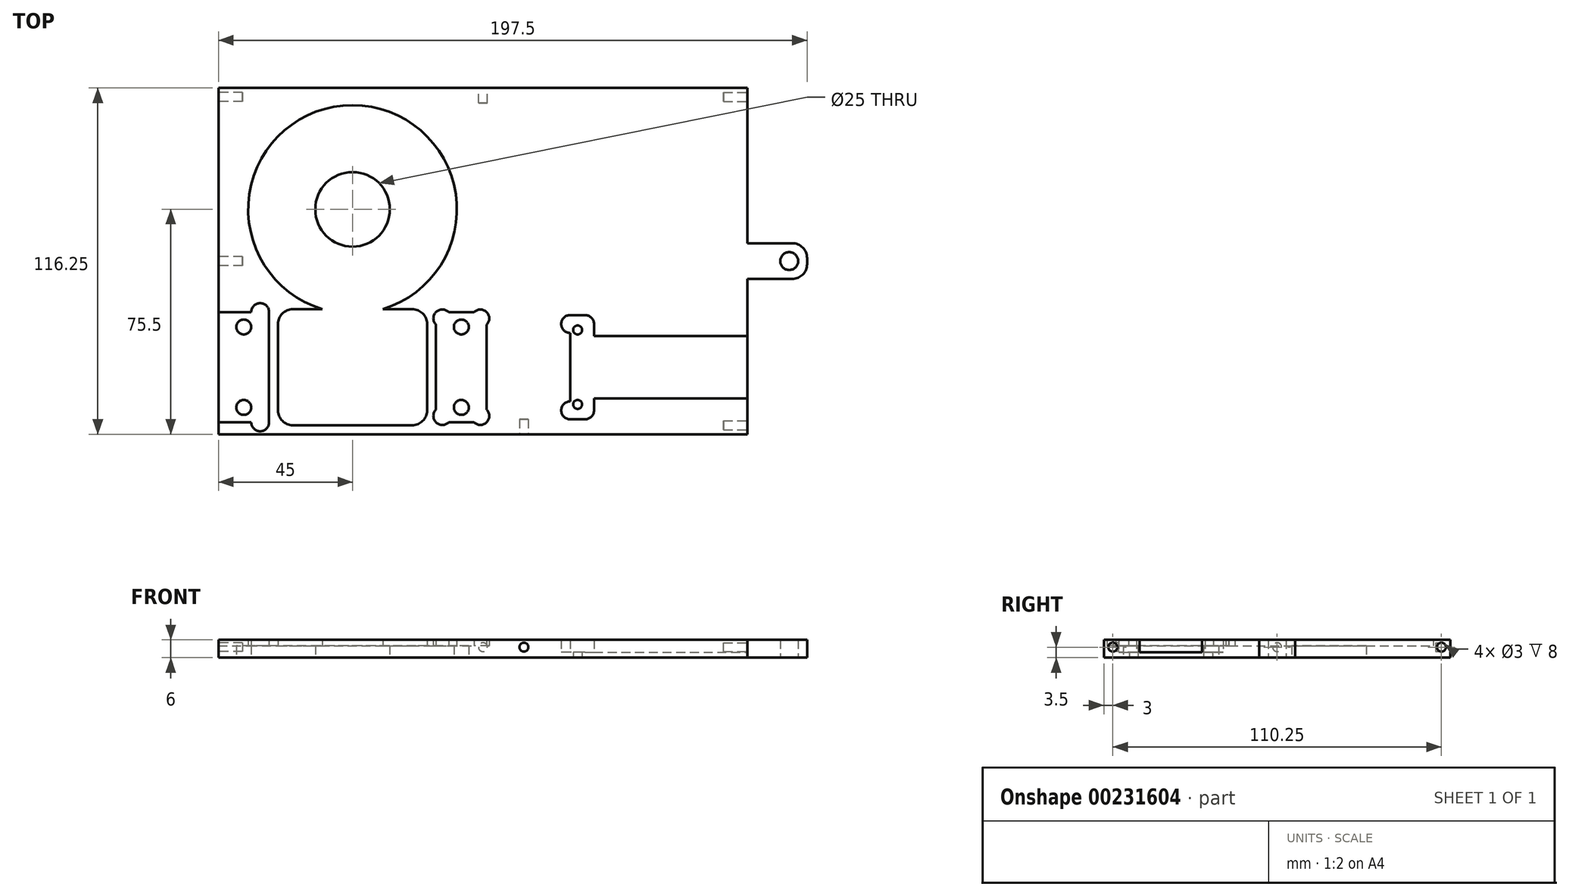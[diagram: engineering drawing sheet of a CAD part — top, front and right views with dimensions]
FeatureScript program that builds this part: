
annotation { "Feature Type Name" : "Feature", "Feature Type Description" : "" }
export const myFeature = defineFeature(function(context is Context, id is Id, definition is map)
    precondition{}
    {
        {
            var Q0;
            Q0=qCreatedBy(makeId("Top.planeOp"),FACE);
            var sketch = newSketch(context, id + "F0", { "sketchPlane" : qUnion([Q0])});
            skLineSegment(sketch, "E0.bottom", {"start": v(0, 0) * mm, "end": v(177.5, 0) * mm});
            skLineSegment(sketch, "E0.top", {"start": v(0, 116.25) * mm, "end": v(177.5, 116.25) * mm});
            skLineSegment(sketch, "E0.left", {"start": v(0, 0) * mm, "end": v(0, 116.25) * mm});
            skLineSegment(sketch, "E0.right", {"start": v(177.5, 0) * mm, "end": v(177.5, 116.25) * mm});
            skCircle(sketch, "E1", {"center": v(45, 75.5) * mm, "radius": 35 * mm});
            skLineSegment(sketch, "E2.right", {"start": v(177.5, 40) * mm, "end": v(177.5, 5) * mm});
            skCircle(sketch, "E3", {"center": v(191.5, 58.12) * mm, "radius": 3 * mm});
            skPoint(sketch, "E3.centerSnap1", {"position": v(191.5, -16.13) * mm});
            skPoint(sketch, "E4", {"position": v(177.5, 22.5) * mm});
            skLineSegment(sketch, "E5.bottom", {"start": v(25, 42) * mm, "end": v(65, 42) * mm});
            skLineSegment(sketch, "E5.top", {"start": v(25, 3) * mm, "end": v(65, 3) * mm});
            skLineSegment(sketch, "E5.left", {"start": v(20, 37) * mm, "end": v(20, 8) * mm});
            skLineSegment(sketch, "E5.right", {"start": v(70, 37) * mm, "end": v(70, 8) * mm});
            skLineSegment(sketch, "E6", {"start": v(70, 22.5) * mm, "end": v(20, 22.5) * mm, "construction": true});
            skLineSegment(sketch, "E7", {"start": v(45, 3) * mm, "end": v(45, 42) * mm, "construction": true});
            skCircle(sketch, "E8", {"center": v(45, 75.5) * mm, "radius": 12.5 * mm});
            skLineSegment(sketch, "E9.bottom", {"start": v(0, 4) * mm, "end": v(11, 4) * mm});
            skLineSegment(sketch, "E9.top", {"start": v(0, 41) * mm, "end": v(11, 41) * mm});
            skLineSegment(sketch, "E9.left", {"start": v(0, 4) * mm, "end": v(0, 41) * mm});
            skLineSegment(sketch, "E9.right", {"start": v(17, 4) * mm, "end": v(17, 41) * mm});
            skPoint(sketch, "E10", {"position": v(17, 22.5) * mm});
            skLineSegment(sketch, "E11.bottom", {"start": v(72.07, 41) * mm, "end": v(73, 41) * mm});
            skLineSegment(sketch, "E11.top", {"start": v(72.07, 4) * mm, "end": v(73, 4) * mm});
            skLineSegment(sketch, "E11.left", {"start": v(73, 36.76) * mm, "end": v(73, 8.24) * mm});
            skLineSegment(sketch, "E11.right", {"start": v(90, 36.76) * mm, "end": v(90, 8.24) * mm});
            skPoint(sketch, "E12", {"position": v(90, 22.5) * mm});
            skLineSegment(sketch, "E13", {"start": v(73, 4) * mm, "end": v(72.07, 4) * mm, "construction": true});
            skLineSegment(sketch, "E14", {"start": v(70, 4) * mm, "end": v(70, 41) * mm, "construction": true});
            skLineSegment(sketch, "E15", {"start": v(70, 41) * mm, "end": v(73, 41) * mm, "construction": true});
            skLineSegment(sketch, "E16", {"start": v(90, 41) * mm, "end": v(93, 41) * mm, "construction": true});
            skLineSegment(sketch, "E17", {"start": v(93, 41) * mm, "end": v(93, 4) * mm, "construction": true});
            skLineSegment(sketch, "E18", {"start": v(93, 4) * mm, "end": v(90, 4) * mm, "construction": true});
            skLineSegment(sketch, "E19.bottom", {"start": v(90, 13.5) * mm, "end": v(115, 13.5) * mm, "construction": true});
            skLineSegment(sketch, "E19.top", {"start": v(90, 31.5) * mm, "end": v(115, 31.5) * mm, "construction": true});
            skLineSegment(sketch, "E19.left", {"start": v(90, 13.5) * mm, "end": v(90, 31.5) * mm, "construction": true});
            skLineSegment(sketch, "E19.right", {"start": v(115, 13.5) * mm, "end": v(115, 31.5) * mm, "construction": true});
            skPoint(sketch, "E20", {"position": v(115, 22.5) * mm});
            skPoint(sketch, "E21", {"position": v(117.97, 22.5) * mm});
            skPoint(sketch, "E22", {"position": v(177.5, 58.12) * mm});
            skLineSegment(sketch, "E23.bottom", {"start": v(177.5, 64.12) * mm, "end": v(197.5, 64.12) * mm});
            skLineSegment(sketch, "E23.top", {"start": v(177.5, 52.12) * mm, "end": v(197.5, 52.12) * mm});
            skLineSegment(sketch, "E23.left", {"start": v(177.5, 64.12) * mm, "end": v(177.5, 52.13) * mm});
            skLineSegment(sketch, "E23.right", {"start": v(197.5, 64.12) * mm, "end": v(197.5, 52.12) * mm});
            skCircle(sketch, "E24", {"center": v(120.5, 10) * mm, "radius": 1.5 * mm});
            skCircle(sketch, "E25", {"center": v(120.5, 35) * mm, "radius": 1.5 * mm});
            skLineSegment(sketch, "E26", {"start": v(81.5, 41) * mm, "end": v(81.5, 4) * mm, "construction": true});
            skLineSegment(sketch, "E27", {"start": v(8.5, 41) * mm, "end": v(8.5, 4) * mm, "construction": true});
            skCircle(sketch, "E28", {"center": v(8.5, 36) * mm, "radius": 2.5 * mm});
            skCircle(sketch, "E29", {"center": v(8.5, 9) * mm, "radius": 2.5 * mm});
            skCircle(sketch, "E30", {"center": v(81.5, 36) * mm, "radius": 2.5 * mm});
            skCircle(sketch, "E31", {"center": v(81.5, 9) * mm, "radius": 2.5 * mm});
            skLineSegment(sketch, "E32", {"start": v(76.54, 37.46) * mm, "end": v(73, 41) * mm, "construction": true});
            skLineSegment(sketch, "E33", {"start": v(90, 22.5) * mm, "end": v(81.5, 22.5) * mm, "construction": true});
            skLineSegment(sketch, "E34", {"start": v(17, 41) * mm, "end": v(9.3, 33.3) * mm, "construction": true});
            skPoint(sketch, "E35.orphan", {"position": v(17, 4) * mm});
            skPoint(sketch, "E36.visualSharp", {"position": v(20, 42) * mm});
            skArc(sketch, "E36.filletArc", {"start": v(25, 42) * mm, "mid": v(21.46, 40.54) * mm, "end": v(20, 37) * mm});
            skPoint(sketch, "E37.visualSharp", {"position": v(70, 42) * mm});
            skArc(sketch, "E37.filletArc", {"start": v(70, 37) * mm, "mid": v(68.54, 40.54) * mm, "end": v(65, 42) * mm});
            skPoint(sketch, "E38.visualSharp", {"position": v(70, 3) * mm});
            skArc(sketch, "E38.filletArc", {"start": v(65, 3) * mm, "mid": v(68.54, 4.46) * mm, "end": v(70, 8) * mm});
            skPoint(sketch, "E39.visualSharp", {"position": v(20, 3) * mm});
            skArc(sketch, "E39.filletArc", {"start": v(20, 8) * mm, "mid": v(21.46, 4.46) * mm, "end": v(25, 3) * mm});
            skCircle(sketch, "E40", {"center": v(45, 75.5) * mm, "radius": 38.75 * mm, "construction": true});
            skPoint(sketch, "E41", {"position": v(45, 114.25) * mm});
            skPoint(sketch, "E42", {"position": v(6.25, 75.5) * mm});
            skPoint(sketch, "E43.orphan", {"position": v(17, 33.43) * mm});
            skPoint(sketch, "E44.orphan", {"position": v(17, 11.57) * mm});
            skArc(sketch, "E45.trimOffspring", {"start": v(17, 41) * mm, "mid": v(14, 44) * mm, "end": v(11, 41) * mm});
            skArc(sketch, "E46.trimOffspring", {"start": v(11, 4) * mm, "mid": v(14, 1) * mm, "end": v(17, 4) * mm});
            skArc(sketch, "E47", {"start": v(77.24, 41) * mm, "mid": v(73, 41) * mm, "end": v(73, 36.76) * mm});
            skPoint(sketch, "E48.orphan", {"position": v(73, 34.71) * mm});
            skLineSegment(sketch, "E49.trimOffspring", {"start": v(77.24, 41) * mm, "end": v(85.76, 41) * mm});
            skPoint(sketch, "E50.orphan", {"position": v(73, 22.5) * mm});
            skArc(sketch, "E51.MirrorCS", {"start": v(77.24, 4) * mm, "mid": v(73, 4) * mm, "end": v(73, 8.24) * mm});
            skArc(sketch, "E52.MirrorCS", {"start": v(85.76, 41) * mm, "mid": v(90, 41) * mm, "end": v(90, 36.76) * mm});
            skArc(sketch, "E53.MirrorCS", {"start": v(85.76, 4) * mm, "mid": v(90, 4) * mm, "end": v(90, 8.24) * mm});
            skPoint(sketch, "E54.orphan", {"position": v(73, 10.29) * mm});
            skPoint(sketch, "E55.orphan", {"position": v(90, 10.29) * mm});
            skPoint(sketch, "E56.orphan", {"position": v(90, 34.71) * mm});
            skLineSegment(sketch, "E57.trimOffspring", {"start": v(90, 41) * mm, "end": v(90.93, 41) * mm});
            skLineSegment(sketch, "E58.trimOffspring", {"start": v(90, 4) * mm, "end": v(90.93, 4) * mm});
            skLineSegment(sketch, "E59.trimOffspring", {"start": v(77.24, 4) * mm, "end": v(85.76, 4) * mm});
            skLineSegment(sketch, "E60", {"start": v(123, 40) * mm, "end": v(123, 11) * mm, "construction": true});
            skLineSegment(sketch, "E61", {"start": v(123, 40) * mm, "end": v(118, 40) * mm});
            skLineSegment(sketch, "E62", {"start": v(123, 5) * mm, "end": v(118, 5) * mm});
            skLineSegment(sketch, "E63", {"start": v(120.5, 5) * mm, "end": v(120.5, 40) * mm, "construction": true});
            skArc(sketch, "E64", {"start": v(118, 11) * mm, "mid": v(115, 8) * mm, "end": v(118, 5) * mm});
            skLineSegment(sketch, "E65.trimOffspring", {"start": v(118, 34) * mm, "end": v(118, 11) * mm});
            skArc(sketch, "E66.trimOffspring", {"start": v(118, 40) * mm, "mid": v(115, 37) * mm, "end": v(118, 34) * mm});
            skArc(sketch, "E67", {"start": v(126, 37) * mm, "mid": v(125.12, 39.12) * mm, "end": v(123, 40) * mm});
            skArc(sketch, "E68", {"start": v(123, 5) * mm, "mid": v(125.12, 5.88) * mm, "end": v(126, 8) * mm});
            skLineSegment(sketch, "E69", {"start": v(126, 12) * mm, "end": v(177.5, 12) * mm});
            skLineSegment(sketch, "E70", {"start": v(126, 33) * mm, "end": v(177.5, 33) * mm});
            skLineSegment(sketch, "E71", {"start": v(123, 34) * mm, "end": v(123, 33) * mm});
            skLineSegment(sketch, "E72", {"start": v(123, 12) * mm, "end": v(123, 11) * mm});
            skLineSegment(sketch, "E73.trimOffspring", {"start": v(123, 8) * mm, "end": v(123, 5) * mm, "construction": true});
            skLineSegment(sketch, "E74", {"start": v(126, 37) * mm, "end": v(126, 33) * mm});
            skLineSegment(sketch, "E75", {"start": v(126, 8) * mm, "end": v(126, 12) * mm});
            skSolve(sketch);
        }
        {
            var Q0;
            Q0=makeQuery(id+"F0.imprint","IMPRINT",FACE,{"disambiguationData":[TD([[makeQuery(id+"F0.imprint","IMPRINT",EDGE,{"derivedFrom":sQuery(id+"F0.wireOp",EDGE,"E0.bottom")}),1.0]])]});
            var Q1;
            Q1=makeQuery(id+"F0.imprint","IMPRINT",FACE,{"disambiguationData":[TD([[makeQuery(id+"F0.imprint","IMPRINT",EDGE,{"derivedFrom":sQuery(id+"F0.wireOp",EDGE,"E3")}),-1.0]])]});
            var Q2;
            {var subQ13=sQuery(id+"F0.wireOp",EDGE,"E0.top");Q2=makeQuery(id+"F0.imprint","IMPRINT",FACE,{"disambiguationData":[TD([[makeQuery(id+"F0.imprint","IMPRINT",EDGE,{"derivedFrom":subQ13}),-1.0]])]});}
            extrude(context, id + "F1", {"entities" : qUnion([Q0, Q1, Q2]), "depth" : 6 * mm});
        }
        {
            var Q0;
            Q0=makeQuery(id+"F0.imprint","IMPRINT",FACE,{"disambiguationData":[TD([[makeQuery(id+"F0.imprint","IMPRINT",EDGE,{"derivedFrom":sQuery(id+"F0.wireOp",EDGE,"E1")}),1.0]])]});
            var Q1;
            Q1=makeQuery(id+"F0.imprint","IMPRINT",FACE,{"disambiguationData":[TD([[makeQuery(id+"F0.imprint","IMPRINT",EDGE,{"derivedFrom":sQuery(id+"F0.wireOp",EDGE,"E8")}),-1.0]])]});
            var Q2;
            Q2=makeQuery(id+"F0.imprint","IMPRINT",FACE,{"disambiguationData":[TD([[makeQuery(id+"F0.imprint","IMPRINT",EDGE,{"derivedFrom":sQuery(id+"F0.wireOp",EDGE,"E9.bottom")}),1.0]])]});
            var Q3;
            {var subQ2=sQuery(id+"F0.wireOp",EDGE,"E11.left");Q3=makeQuery(id+"F0.imprint","IMPRINT",FACE,{"disambiguationData":[TD([[makeQuery(id+"F0.imprint","IMPRINT",EDGE,{"derivedFrom":subQ2}),1.0]])]});}
            var Q4;
            Q4=makeQuery(id+"F0.imprint","IMPRINT",FACE,{"disambiguationData":[TD([[makeQuery(id+"F0.imprint","IMPRINT",EDGE,{"derivedFrom":sQuery(id+"F0.wireOp",EDGE,"E2.bottom")}),-1.0]])]});
            var Q5;
            Q5=makeQuery(id+"F0.imprint","IMPRINT",FACE,{"disambiguationData":[TD([[makeQuery(id+"F0.imprint","IMPRINT",EDGE,{"derivedFrom":sQuery(id+"F0.wireOp",EDGE,"E5.top")}),1.0]])]});
            extrude(context, id + "F2", {"entities" : qUnion([Q0, Q1, Q2, Q3, Q4, Q5]), "operationType" : NewBodyOperationType.ADD, "depth" : 4 * mm});
        }
        {
            var Q0;
            Q0=makeQuery(id+"F0.imprint","IMPRINT",FACE,{"disambiguationData":[TD([[makeQuery(id+"F0.imprint","IMPRINT",EDGE,{"derivedFrom":sQuery(id+"F0.wireOp",EDGE,"E5.bottom")}),-1.0]])]});
            extrude(context, id + "F3", {"entities" : qUnion([Q0]), "operationType" : NewBodyOperationType.ADD, "depth" : 2 * mm});
        }
        {
            var Q0;
            Q0=makeQuery(id+"F0.imprint","IMPRINT",FACE,{"disambiguationData":[TD([[makeQuery(id+"F0.imprint","IMPRINT",EDGE,{"derivedFrom":sQuery(id+"F0.wireOp",EDGE,"E9.bottom")}),1.0]])]});
            var Q1;
            Q1=makeQuery(id+"F0.imprint","IMPRINT",FACE,{"disambiguationData":[TD([[makeQuery(id+"F0.imprint","IMPRINT",EDGE,{"derivedFrom":sQuery(id+"F0.wireOp",EDGE,"E11.bottom")}),-1.0]])]});
            extrude(context, id + "F4", {"entities" : qUnion([Q0, Q1]), "operationType" : NewBodyOperationType.ADD, "depth" : 3 * mm});
        }
        {
            var Q0;
            {var subQ3=sQuery(id+"F0.wireOp",EDGE,"E2.bottom");Q0=makeQuery(id+"F0.imprint","IMPRINT",FACE,{"disambiguationData":[TD([[makeQuery(id+"F0.imprint","IMPRINT",EDGE,{"derivedFrom":subQ3}),-1.0]])]});}
            var Q1;
            Q1=makeQuery(id+"F0.imprint","IMPRINT",FACE,{"disambiguationData":[TD([[makeQuery(id+"F0.imprint","IMPRINT",EDGE,{"derivedFrom":sQuery(id+"F0.wireOp",EDGE,"uMl3fZDs-IYx8-yGXx-dg1t-XEFDvq9bwMY9.bottom")}),1.0]])]});
            var Q2;
            Q2=makeQuery(id+"F0.imprint","IMPRINT",FACE,{"disambiguationData":[TD([[makeQuery(id+"F0.imprint","IMPRINT",EDGE,{"derivedFrom":sQuery(id+"F0.wireOp",EDGE,"E24")}),-1.0]])]});
            var Q3;
            Q3=sQuery(id+"F0.wireOp",EDGE,"E2.left");
            var Q4;
            Q4=sQuery(id+"F0.wireOp",EDGE,"E2.top");
            var Q5;
            Q5=sQuery(id+"F0.wireOp",EDGE,"E2.right");
            var Q6;
            Q6=sQuery(id+"F0.wireOp",EDGE,"E2.bottom");
            extrude(context, id + "F5", {"entities" : qUnion([Q0, Q1, Q2]), "operationType" : NewBodyOperationType.ADD, "surfaceEntities" : qUnion([Q3, Q4, Q5, Q6]), "depth" : 1.75 * mm});
        }
        {
            var Q0;
            {var subQ0=sQuery(id+"F0.wireOp",EDGE,"E0.right");Q0=makeQuery(id+"F1.opExtrude","SWEPT_FACE",FACE,{"disambiguationData":[OSD([subQ0]),TDD([makeQuery(id+"F0.imprint","IMPRINT",EDGE,{"disambiguationData":[TD([[makeQuery(id+"F0.imprint","INTERSECT",VERTEX,{"derivedFrom":[sQuery(id+"F0.wireOp",EDGE,"E0.top"),subQ0]}),1.0]])],"derivedFrom":subQ0})])]});}
            var sketch = newSketch(context, id + "F6", { "sketchPlane" : qUnion([Q0])});
            skLineSegment(sketch, "E76", {"start": v(0, 3.5) * mm, "end": v(116.25, 3.5) * mm, "construction": true});
            skCircle(sketch, "E77", {"center": v(3, 3.5) * mm, "radius": 1.5 * mm});
            skCircle(sketch, "E78", {"center": v(113.25, 3.5) * mm, "radius": 1.5 * mm});
            skSolve(sketch);
        }
        {
            var Q0;
            Q0 = qSketchRegion(id + "F6", true);
            extrude(context, id + "F7", {"entities" : qUnion([Q0]), "operationType" : NewBodyOperationType.REMOVE, "oppositeDirection" : true, "depth" : 8 * mm});
        }
        {
            var Q0;
            {var subQ0=sQuery(id+"F0.wireOp",EDGE,"E9.left");var subQ1=sQuery(id+"F0.wireOp",EDGE,"E0.left");Q0=makeQuery(id+"F4.boolean.opBoolean","MERGE",FACE,{"derivedFrom":[makeQuery(id+"F1.opExtrude","SWEPT_FACE",FACE,{"disambiguationData":[OSD([subQ1]),TDD([makeQuery(id+"F0.imprint","IMPRINT",EDGE,{"disambiguationData":[TD([[makeQuery(id+"F0.imprint","INTERSECT",VERTEX,{"derivedFrom":[sQuery(id+"F0.wireOp",EDGE,"E0.bottom"),subQ1]}),-1.0]])],"derivedFrom":subQ1})])]}),makeQuery(id+"F1.opExtrude","SWEPT_FACE",FACE,{"disambiguationData":[OSD([subQ1]),TDD([makeQuery(id+"F0.imprint","IMPRINT",EDGE,{"disambiguationData":[TD([[makeQuery(id+"F0.imprint","INTERSECT",VERTEX,{"derivedFrom":[sQuery(id+"F0.wireOp",EDGE,"E0.top"),subQ1]}),1.0]])],"derivedFrom":subQ1})])]}),makeQuery(id+"F4.opExtrude","SWEPT_FACE",FACE,{"disambiguationData":[OSD([subQ0])]})]});}
            var sketch = newSketch(context, id + "F8", { "sketchPlane" : qUnion([Q0])});
            skLineSegment(sketch, "E79", {"start": v(-116.25, 3.5) * mm, "end": v(0, 3.5) * mm, "construction": true});
            skCircle(sketch, "E80", {"center": v(-113.25, 3.5) * mm, "radius": 1.5 * mm});
            skPoint(sketch, "E81", {"position": v(-58.12, 3.5) * mm});
            skCircle(sketch, "E82", {"center": v(-58.12, 3.5) * mm, "radius": 1.5 * mm});
            skSolve(sketch);
        }
        {
            var Q0;
            Q0 = qSketchRegion(id + "F8", true);
            extrude(context, id + "F9", {"entities" : qUnion([Q0]), "operationType" : NewBodyOperationType.REMOVE, "oppositeDirection" : true, "depth" : 8 * mm});
        }
        {
            var Q0;
            Q0=makeQuery(id+"F1.opExtrude","SWEPT_FACE",FACE,{"disambiguationData":[OSD([sQuery(id+"F0.wireOp",EDGE,"E0.bottom")])]});
            var sketch = newSketch(context, id + "F10", { "sketchPlane" : qUnion([Q0])});
            skLineSegment(sketch, "E83", {"start": v(0, 3.5) * mm, "end": v(177.5, 3.5) * mm, "construction": true});
            skCircle(sketch, "E84", {"center": v(102.5, 3.5) * mm, "radius": 1.5 * mm});
            skSolve(sketch);
        }
        {
            var Q0;
            Q0 = qSketchRegion(id + "F10", true);
            extrude(context, id + "F11", {"entities" : qUnion([Q0]), "operationType" : NewBodyOperationType.REMOVE, "oppositeDirection" : true, "depth" : 5 * mm});
        }
        {
            var Q0;
            Q0=makeQuery(id+"F1.opExtrude","SWEPT_FACE",FACE,{"disambiguationData":[OSD([sQuery(id+"F0.wireOp",EDGE,"E0.top")])]});
            var sketch = newSketch(context, id + "F12", { "sketchPlane" : qUnion([Q0])});
            skLineSegment(sketch, "E85", {"start": v(-177.5, 3.5) * mm, "end": v(0, 3.5) * mm, "construction": true});
            skCircle(sketch, "E86", {"center": v(-88.75, 3.5) * mm, "radius": 1.5 * mm});
            skSolve(sketch);
        }
        {
            var Q0;
            Q0 = qSketchRegion(id + "F12", true);
            extrude(context, id + "F13", {"entities" : qUnion([Q0]), "operationType" : NewBodyOperationType.REMOVE, "oppositeDirection" : true, "depth" : 5 * mm});
        }
        {
            var Q0;
            Q0=makeQuery(id+"F1.opExtrude","SWEPT_EDGE",EDGE,{"disambiguationData":[OSD([sQuery(id+"F0.wireOp",EDGE,"E23.top"),sQuery(id+"F0.wireOp",EDGE,"E23.right")])]});
            var Q1;
            Q1=makeQuery(id+"F1.opExtrude","SWEPT_EDGE",EDGE,{"disambiguationData":[OSD([sQuery(id+"F0.wireOp",EDGE,"E23.bottom"),sQuery(id+"F0.wireOp",EDGE,"E23.right")])]});
            fillet(context, id + "F14", {"entities" : qUnion([Q0, Q1]), "radius" : 5 * mm, "tangentPropagation" : true, "allowEdgeOverflow" : false});
        }
    });
